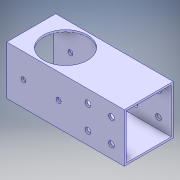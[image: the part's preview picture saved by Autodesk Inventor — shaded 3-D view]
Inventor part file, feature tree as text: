
AUTODESK INVENTOR PART (.ipt)
format: ipt  version: 2018 (Build 220112000, 112)  size: 164,864 bytes
history: native  units: mm
features: other x2, extrude x2, sketch x2
ambient origin geometry x8: Origin, YZ Plane, XZ Plane, XY Plane, X Axis, Y Axis, Z Axis, Center Point
bodies: Body1 (feature_tree)
feature tree (6):
  other  "ソリッド1"
  extrude  "押し出し1"  Depth=50.0mm
  extrude  "押し出し2"  Depth=10.0mm TaperAngle=0.0deg
  sketch  "スケッチ1"
  sketch  "スケッチ2"
  other  "PartBody"
